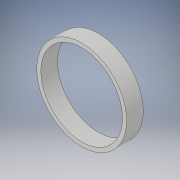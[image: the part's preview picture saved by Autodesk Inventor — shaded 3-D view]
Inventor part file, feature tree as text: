
AUTODESK INVENTOR PART (.ipt)
format: ipt  version: 2019 (Build 230136000, 136)  size: 105,472 bytes
history: native  units: mm
features: extrude x2, sketch x2
ambient origin geometry x8: Origin, YZ Plane, XZ Plane, XY Plane, X Axis, Y Axis, Z Axis, Center Point
bodies: Solid1 (feature_tree)
feature tree (4):
  extrude  "Extrusion1"  Depth=1.74mm TaperAngle=0.0deg
  extrude  "Extrusion2"  Depth=1.74mm TaperAngle=0.0deg
  sketch  "Sketch1"  dims[d0=9.42mm d1=1.74mm d2=0.0mm]
  sketch  "Sketch2"  dims[d3=8.56mm d4=1.74mm d5=0.0mm]
